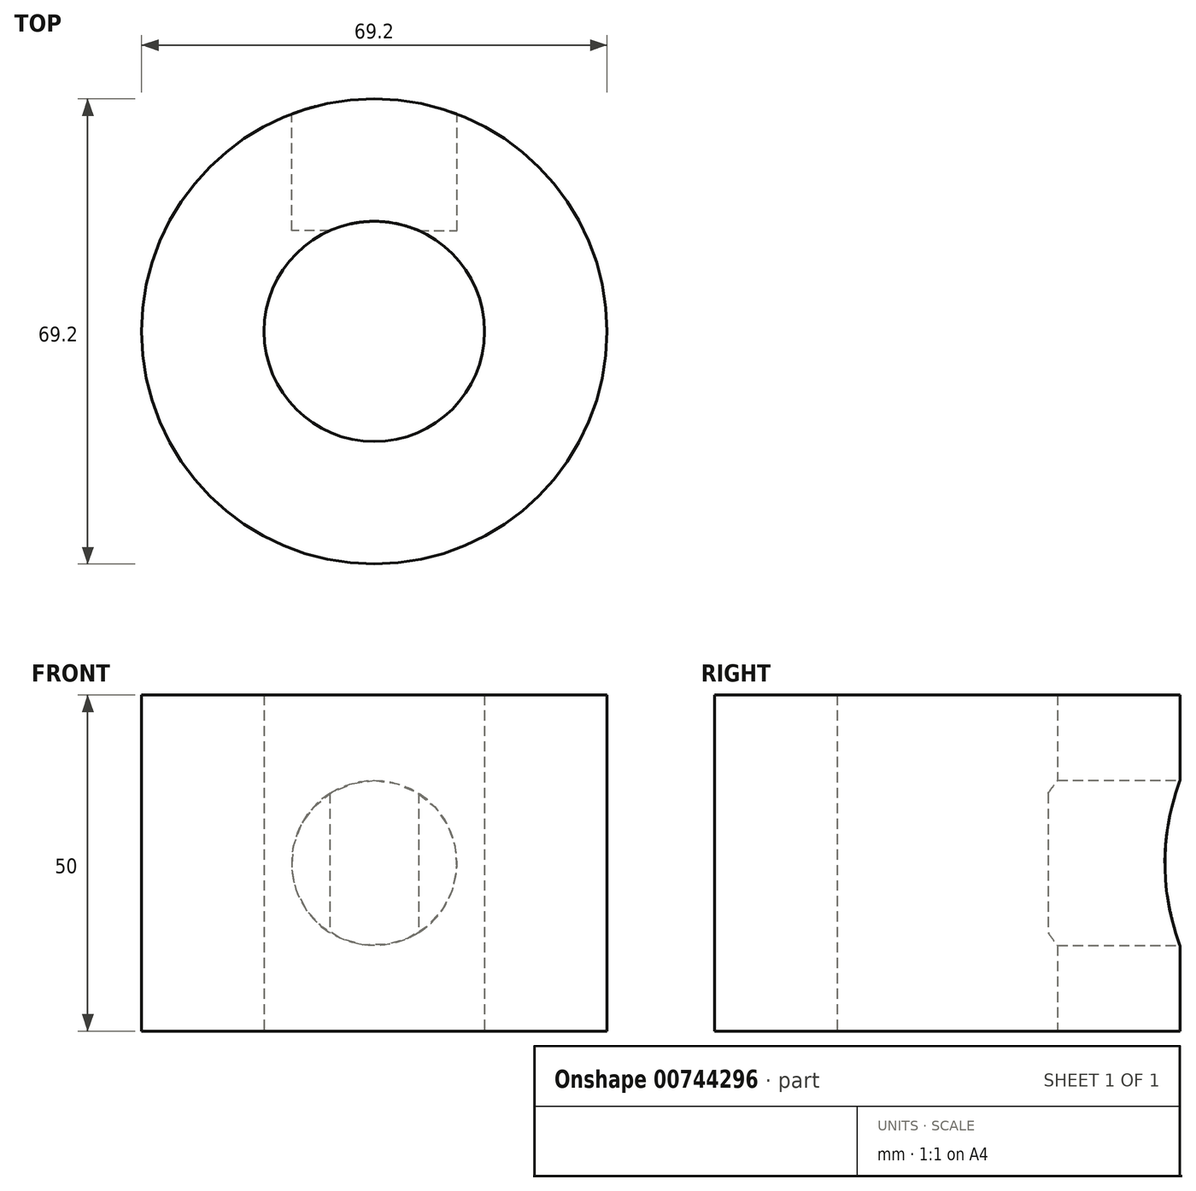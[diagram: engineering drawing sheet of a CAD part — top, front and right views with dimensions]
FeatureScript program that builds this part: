
annotation { "Feature Type Name" : "Feature", "Feature Type Description" : "" }
export const myFeature = defineFeature(function(context is Context, id is Id, definition is map)
    precondition{}
    {
        {
            var Q0;
            Q0=qCreatedBy(makeId("Top.planeOp"),FACE);
            var sketch = newSketch(context, id + "F0", { "sketchPlane" : qUnion([Q0])});
            skCircle(sketch, "E0", {"center": v(0, 0) * mm, "radius": 34.6 * mm});
            skCircle(sketch, "E1", {"center": v(0, 0) * mm, "radius": 16.38 * mm});
            skSolve(sketch);
        }
        {
            var Q0;
            Q0 = qSketchRegion(id + "F0", true);
            extrude(context, id + "F1", {"entities" : qUnion([Q0]), "depth" : 25 * mm, "offsetDistance" : 25 * mm, "hasSecondDirection" : true, "secondDirectionOppositeDirection" : true, "secondDirectionDepth" : 25 * mm});
        }
        {
            var Q0;
            Q0=qCreatedBy(makeId("Front.planeOp"),FACE);
            cPlane(context, id + "F2", {"entities" : qUnion([Q0]), "cplaneType" : CPlaneType.OFFSET, "offset" : 40 * mm, "oppositeDirection" : true, "width" : 150 * mm, "height" : 150 * mm});
        }
        {
            var Q0;
            Q0=qCreatedBy(id+"F2.planeOp",FACE);
            var sketch = newSketch(context, id + "F3", { "sketchPlane" : qUnion([Q0])});
            skCircle(sketch, "E2", {"center": v(0, 0) * mm, "radius": 12.28 * mm});
            skSolve(sketch);
        }
        {
            var Q0;
            Q0 = qSketchRegion(id + "F3", true);
            extrude(context, id + "F4", {"entities" : qUnion([Q0]), "operationType" : NewBodyOperationType.REMOVE, "depth" : 25 * mm, "offsetDistance" : 25 * mm});
        }
    });
